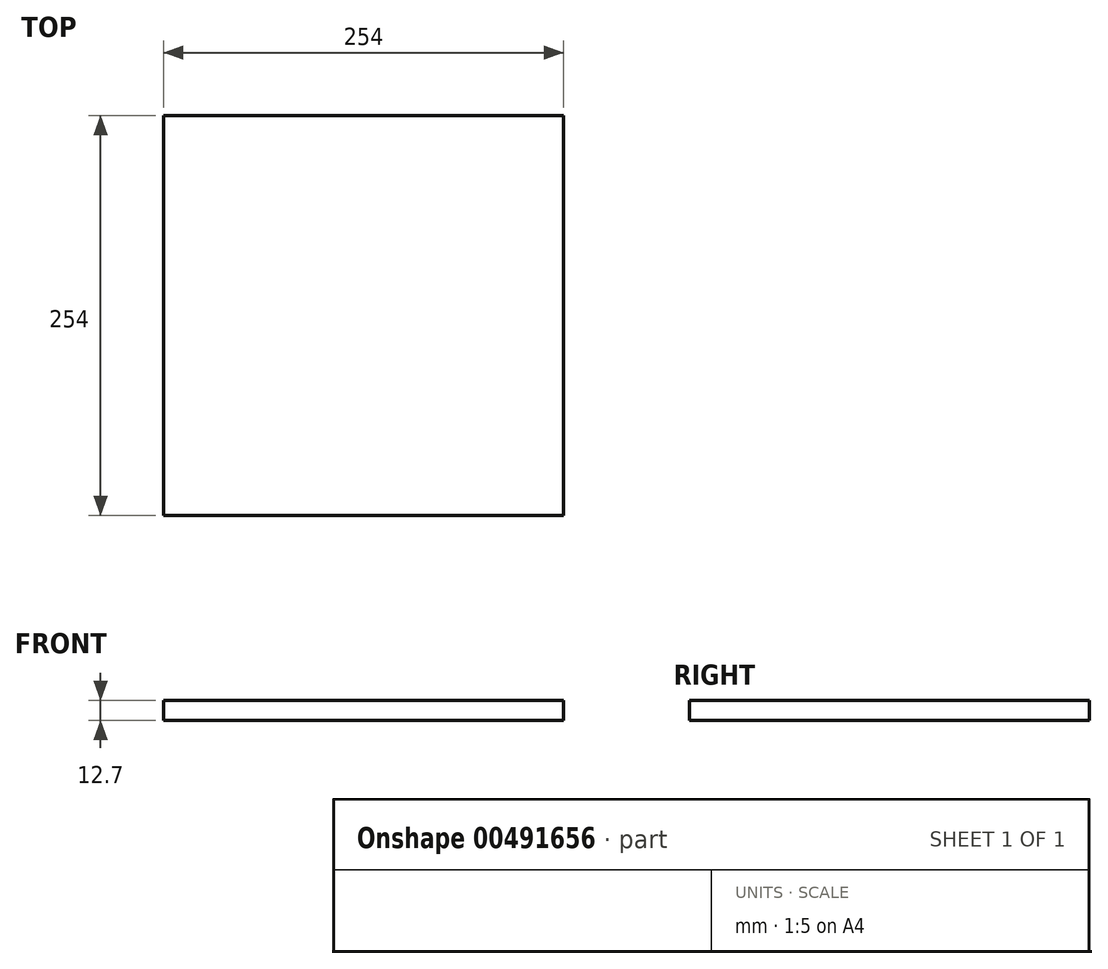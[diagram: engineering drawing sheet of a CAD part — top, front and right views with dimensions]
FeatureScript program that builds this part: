
annotation { "Feature Type Name" : "Feature", "Feature Type Description" : "" }
export const myFeature = defineFeature(function(context is Context, id is Id, definition is map)
    precondition{}
    {
        {
            var Q0;
            Q0=qCreatedBy(makeId("Top.planeOp"),FACE);
            var sketch = newSketch(context, id + "F0", { "sketchPlane" : qUnion([Q0])});
            skLineSegment(sketch, "E0", {"start": v(-123.31, 128.72) * mm, "end": v(130.69, 128.72) * mm});
            skLineSegment(sketch, "E1", {"start": v(130.69, 128.72) * mm, "end": v(130.69, -125.28) * mm});
            skLineSegment(sketch, "E2", {"start": v(130.69, -125.28) * mm, "end": v(-123.31, -125.28) * mm});
            skLineSegment(sketch, "E3", {"start": v(-123.31, -125.28) * mm, "end": v(-123.31, 128.72) * mm});
            skSolve(sketch);
        }
        {
            var Q0;
            Q0=makeQuery(id+"F0.imprint","IMPRINT",FACE,{"disambiguationData":[TD([[makeQuery(id+"F0.imprint","IMPRINT",EDGE,{"derivedFrom":sQuery(id+"F0.wireOp",EDGE,"E0")}),-1.0]])]});
            var Q1;
            Q1 = qSketchRegion(id + "F0", true);
            extrude(context, id + "F1", {"entities" : qUnion([Q0, Q1]), "depth" : 12.7 * mm});
        }
    });
